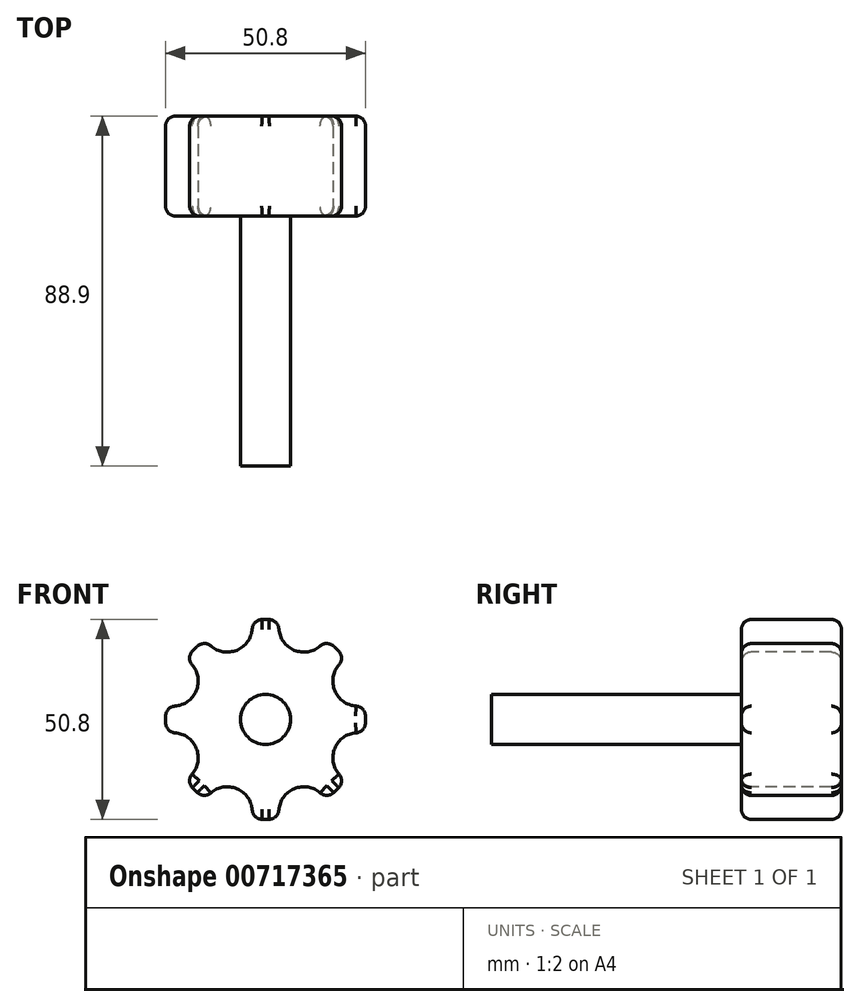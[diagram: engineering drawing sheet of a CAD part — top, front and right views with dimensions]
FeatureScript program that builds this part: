
annotation { "Feature Type Name" : "Feature", "Feature Type Description" : "" }
export const myFeature = defineFeature(function(context is Context, id is Id, definition is map)
    precondition{}
    {
        {
            var Q0;
            Q0=qCreatedBy(makeId("Front.planeOp"),FACE);
            var sketch = newSketch(context, id + "F0", { "sketchPlane" : qUnion([Q0])});
            skCircle(sketch, "E0", {"center": v(0, 0) * mm, "radius": 6.35 * mm});
            skSolve(sketch);
        }
        {
            var Q0;
            Q0=makeQuery(id+"F0.imprint","IMPRINT",FACE,{"disambiguationData":[TD([[makeQuery(id+"F0.imprint","IMPRINT",EDGE,{"derivedFrom":sQuery(id+"F0.wireOp",EDGE,"E0")}),1.0]])]});
            extrude(context, id + "F1", {"entities" : qUnion([Q0]), "depth" : 63.5 * mm, "offsetDistance" : 25.4 * mm});
        }
        {
            var Q0;
            Q0=makeQuery(id+"F1.opExtrude","CAP_FACE",FACE,{"disambiguationData":[OSD([sQuery(id+"F0.wireOp",EDGE,"E0")])],"isStart":true});
            var sketch = newSketch(context, id + "F2", { "sketchPlane" : qUnion([Q0])});
            skCircle(sketch, "E1", {"center": v(0, 0) * mm, "radius": 25.4 * mm});
            skCircle(sketch, "E2", {"center": v(-9.72, 23.46) * mm, "radius": 6.35 * mm});
            skCircle(sketch, "E3", {"center": v(9.72, -23.46) * mm, "radius": 6.35 * mm});
            skLineSegment(sketch, "E4", {"start": v(-9.72, 23.46) * mm, "end": v(9.72, -23.46) * mm, "construction": true});
            skLineSegment(sketch, "E5", {"start": v(-23.46, -9.72) * mm, "end": v(23.46, 9.72) * mm, "construction": true});
            skCircle(sketch, "E6", {"center": v(-23.46, -9.72) * mm, "radius": 6.35 * mm});
            skCircle(sketch, "E7", {"center": v(23.46, 9.72) * mm, "radius": 6.35 * mm});
            skCircle(sketch, "E8", {"center": v(-23.46, 9.72) * mm, "radius": 6.35 * mm});
            skLineSegment(sketch, "E9", {"start": v(-23.46, -9.72) * mm, "end": v(-9.72, -23.46) * mm, "construction": true});
            skLineSegment(sketch, "E10", {"start": v(-9.72, -23.46) * mm, "end": v(9.72, -23.46) * mm, "construction": true});
            skLineSegment(sketch, "E11", {"start": v(9.72, -23.46) * mm, "end": v(23.46, -9.72) * mm, "construction": true});
            skLineSegment(sketch, "E12", {"start": v(23.46, -9.72) * mm, "end": v(23.46, 9.72) * mm, "construction": true});
            skLineSegment(sketch, "E13", {"start": v(23.46, 9.72) * mm, "end": v(9.72, 23.46) * mm, "construction": true});
            skCircle(sketch, "E14", {"center": v(-9.72, -23.46) * mm, "radius": 6.35 * mm});
            skCircle(sketch, "E15", {"center": v(23.46, -9.72) * mm, "radius": 6.35 * mm});
            skCircle(sketch, "E16", {"center": v(9.72, 23.46) * mm, "radius": 6.35 * mm});
            skSolve(sketch);
        }
        {
            var Q0;
            Q0=makeQuery(id+"F2.imprint","IMPRINT",FACE,{"disambiguationData":[TD([[makeQuery(id+"F2.imprint","IMPRINT",EDGE,{"derivedFrom":makeQuery(id+"F1.opExtrude","CAP_EDGE",EDGE,{"disambiguationData":[OSD([sQuery(id+"F0.wireOp",EDGE,"E0")])],"isStart":true})}),1.0]])]});
            var Q1;
            Q1=makeQuery(id+"F2.imprint","IMPRINT",FACE,{"disambiguationData":[TD([[makeQuery(id+"F2.imprint","IMPRINT",EDGE,{"derivedFrom":makeQuery(id+"F1.opExtrude","CAP_EDGE",EDGE,{"disambiguationData":[OSD([sQuery(id+"F0.wireOp",EDGE,"E0")])],"isStart":true})}),-1.0]])]});
            extrude(context, id + "F3", {"entities" : qUnion([Q0, Q1]), "operationType" : NewBodyOperationType.ADD, "depth" : 25.4 * mm, "offsetDistance" : 25.4 * mm});
        }
        {
            var Q0;
            Q0=makeQuery(id+"F3.opExtrude","CAP_EDGE",EDGE,{"disambiguationData":[OSD([sQuery(id+"F2.wireOp",EDGE,"E6")])],"isStart":false});
            var Q1;
            Q1=makeQuery(id+"F3.opExtrude","CAP_EDGE",EDGE,{"disambiguationData":[OSD([sQuery(id+"F2.wireOp",EDGE,"E14")])],"isStart":false});
            var Q2;
            {var subQ0=sQuery(id+"F2.wireOp",EDGE,"E1");Q2=makeQuery(id+"F3.opExtrude","CAP_EDGE",EDGE,{"disambiguationData":[OSD([subQ0]),TDD([makeQuery(id+"F2.imprint","IMPRINT",EDGE,{"disambiguationData":[TD([[makeQuery(id+"F2.imprint","INTERSECT",VERTEX,{"disambiguationData":[OD(1.0)],"derivedFrom":[subQ0,sQuery(id+"F2.wireOp",EDGE,"E6")]}),-1.0]])],"derivedFrom":subQ0})])],"isStart":false});}
            var Q3;
            Q3=makeQuery(id+"F3.opExtrude","CAP_EDGE",EDGE,{"disambiguationData":[OSD([sQuery(id+"F2.wireOp",EDGE,"E3")])],"isStart":false});
            var Q4;
            Q4=makeQuery(id+"F3.opExtrude","CAP_EDGE",EDGE,{"disambiguationData":[OSD([sQuery(id+"F2.wireOp",EDGE,"E15")])],"isStart":false});
            var Q5;
            Q5=makeQuery(id+"F3.opExtrude","CAP_EDGE",EDGE,{"disambiguationData":[OSD([sQuery(id+"F2.wireOp",EDGE,"E8")])],"isStart":false});
            var Q6;
            Q6=makeQuery(id+"F3.opExtrude","CAP_EDGE",EDGE,{"disambiguationData":[OSD([sQuery(id+"F2.wireOp",EDGE,"E7")])],"isStart":false});
            var Q7;
            Q7=makeQuery(id+"F3.opExtrude","CAP_EDGE",EDGE,{"disambiguationData":[OSD([sQuery(id+"F2.wireOp",EDGE,"E2")])],"isStart":false});
            var Q8;
            Q8=makeQuery(id+"F3.opExtrude","CAP_EDGE",EDGE,{"disambiguationData":[OSD([sQuery(id+"F2.wireOp",EDGE,"E16")])],"isStart":false});
            var Q9;
            {var subQ0=sQuery(id+"F2.wireOp",EDGE,"E1");Q9=makeQuery(id+"F3.opExtrude","CAP_EDGE",EDGE,{"disambiguationData":[OSD([subQ0]),TDD([makeQuery(id+"F2.imprint","IMPRINT",EDGE,{"disambiguationData":[TD([[makeQuery(id+"F2.imprint","INTERSECT",VERTEX,{"disambiguationData":[OD(1.0)],"derivedFrom":[subQ0,sQuery(id+"F2.wireOp",EDGE,"E3")]}),-1.0]])],"derivedFrom":subQ0})])],"isStart":false});}
            var Q10;
            {var subQ0=sQuery(id+"F2.wireOp",EDGE,"E1");Q10=makeQuery(id+"F3.opExtrude","CAP_EDGE",EDGE,{"disambiguationData":[OSD([subQ0]),TDD([makeQuery(id+"F2.imprint","IMPRINT",EDGE,{"disambiguationData":[TD([[makeQuery(id+"F2.imprint","INTERSECT",VERTEX,{"disambiguationData":[OD(1.0)],"derivedFrom":[subQ0,sQuery(id+"F2.wireOp",EDGE,"E7")]}),1.0]])],"derivedFrom":subQ0})])],"isStart":false});}
            var Q11;
            {var subQ0=sQuery(id+"F2.wireOp",EDGE,"E1");Q11=makeQuery(id+"F3.opExtrude","CAP_EDGE",EDGE,{"disambiguationData":[OSD([subQ0]),TDD([makeQuery(id+"F2.imprint","IMPRINT",EDGE,{"disambiguationData":[TD([[makeQuery(id+"F2.imprint","INTERSECT",VERTEX,{"disambiguationData":[OD(0.0)],"derivedFrom":[subQ0,sQuery(id+"F2.wireOp",EDGE,"E7")]}),-1.0]])],"derivedFrom":subQ0})])],"isStart":false});}
            var Q12;
            {var subQ0=sQuery(id+"F2.wireOp",EDGE,"E1");Q12=makeQuery(id+"F3.opExtrude","CAP_EDGE",EDGE,{"disambiguationData":[OSD([subQ0]),TDD([makeQuery(id+"F2.imprint","IMPRINT",EDGE,{"disambiguationData":[TD([[makeQuery(id+"F2.imprint","INTERSECT",VERTEX,{"disambiguationData":[OD(1.0)],"derivedFrom":[subQ0,sQuery(id+"F2.wireOp",EDGE,"E16")]}),-1.0]])],"derivedFrom":subQ0})])],"isStart":false});}
            var Q13;
            {var subQ0=sQuery(id+"F2.wireOp",EDGE,"E1");Q13=makeQuery(id+"F3.opExtrude","CAP_EDGE",EDGE,{"disambiguationData":[OSD([subQ0]),TDD([makeQuery(id+"F2.imprint","IMPRINT",EDGE,{"disambiguationData":[TD([[makeQuery(id+"F2.imprint","INTERSECT",VERTEX,{"disambiguationData":[OD(1.0)],"derivedFrom":[subQ0,sQuery(id+"F2.wireOp",EDGE,"E14")]}),-1.0]])],"derivedFrom":subQ0})])],"isStart":false});}
            var Q14;
            {var subQ0=sQuery(id+"F2.wireOp",EDGE,"E1");Q14=makeQuery(id+"F3.opExtrude","CAP_EDGE",EDGE,{"disambiguationData":[OSD([subQ0]),TDD([makeQuery(id+"F2.imprint","IMPRINT",EDGE,{"disambiguationData":[TD([[makeQuery(id+"F2.imprint","INTERSECT",VERTEX,{"disambiguationData":[OD(1.0)],"derivedFrom":[subQ0,sQuery(id+"F2.wireOp",EDGE,"E8")]}),-1.0]])],"derivedFrom":subQ0})])],"isStart":false});}
            var Q15;
            {var subQ0=sQuery(id+"F2.wireOp",EDGE,"E1");Q15=makeQuery(id+"F3.opExtrude","CAP_EDGE",EDGE,{"disambiguationData":[OSD([subQ0]),TDD([makeQuery(id+"F2.imprint","IMPRINT",EDGE,{"disambiguationData":[TD([[makeQuery(id+"F2.imprint","INTERSECT",VERTEX,{"disambiguationData":[OD(1.0)],"derivedFrom":[subQ0,sQuery(id+"F2.wireOp",EDGE,"E2")]}),-1.0]])],"derivedFrom":subQ0})])],"isStart":false});}
            var Q16;
            {var subQ0=sQuery(id+"F2.wireOp",EDGE,"E1");Q16=makeQuery(id+"F3.opExtrude","CAP_EDGE",EDGE,{"disambiguationData":[OSD([subQ0]),TDD([makeQuery(id+"F2.imprint","IMPRINT",EDGE,{"disambiguationData":[TD([[makeQuery(id+"F2.imprint","INTERSECT",VERTEX,{"disambiguationData":[OD(1.0)],"derivedFrom":[subQ0,sQuery(id+"F2.wireOp",EDGE,"E7")]}),1.0]])],"derivedFrom":subQ0})])],"isStart":true});}
            var Q17;
            Q17=makeQuery(id+"F3.opExtrude","CAP_EDGE",EDGE,{"disambiguationData":[OSD([sQuery(id+"F2.wireOp",EDGE,"E15")])],"isStart":true});
            var Q18;
            {var subQ0=sQuery(id+"F2.wireOp",EDGE,"E1");Q18=makeQuery(id+"F3.opExtrude","CAP_EDGE",EDGE,{"disambiguationData":[OSD([subQ0]),TDD([makeQuery(id+"F2.imprint","IMPRINT",EDGE,{"disambiguationData":[TD([[makeQuery(id+"F2.imprint","INTERSECT",VERTEX,{"disambiguationData":[OD(1.0)],"derivedFrom":[subQ0,sQuery(id+"F2.wireOp",EDGE,"E3")]}),-1.0]])],"derivedFrom":subQ0})])],"isStart":true});}
            var Q19;
            Q19=makeQuery(id+"F3.opExtrude","CAP_EDGE",EDGE,{"disambiguationData":[OSD([sQuery(id+"F2.wireOp",EDGE,"E3")])],"isStart":true});
            var Q20;
            {var subQ0=sQuery(id+"F2.wireOp",EDGE,"E1");Q20=makeQuery(id+"F3.opExtrude","CAP_EDGE",EDGE,{"disambiguationData":[OSD([subQ0]),TDD([makeQuery(id+"F2.imprint","IMPRINT",EDGE,{"disambiguationData":[TD([[makeQuery(id+"F2.imprint","INTERSECT",VERTEX,{"disambiguationData":[OD(1.0)],"derivedFrom":[subQ0,sQuery(id+"F2.wireOp",EDGE,"E14")]}),-1.0]])],"derivedFrom":subQ0})])],"isStart":true});}
            var Q21;
            Q21=makeQuery(id+"F3.opExtrude","CAP_EDGE",EDGE,{"disambiguationData":[OSD([sQuery(id+"F2.wireOp",EDGE,"E14")])],"isStart":true});
            var Q22;
            Q22=makeQuery(id+"F3.opExtrude","CAP_EDGE",EDGE,{"disambiguationData":[OSD([sQuery(id+"F2.wireOp",EDGE,"E7")])],"isStart":true});
            var Q23;
            {var subQ0=sQuery(id+"F2.wireOp",EDGE,"E1");Q23=makeQuery(id+"F3.opExtrude","CAP_EDGE",EDGE,{"disambiguationData":[OSD([subQ0]),TDD([makeQuery(id+"F2.imprint","IMPRINT",EDGE,{"disambiguationData":[TD([[makeQuery(id+"F2.imprint","INTERSECT",VERTEX,{"disambiguationData":[OD(0.0)],"derivedFrom":[subQ0,sQuery(id+"F2.wireOp",EDGE,"E7")]}),-1.0]])],"derivedFrom":subQ0})])],"isStart":true});}
            var Q24;
            Q24=makeQuery(id+"F3.opExtrude","CAP_EDGE",EDGE,{"disambiguationData":[OSD([sQuery(id+"F2.wireOp",EDGE,"E16")])],"isStart":true});
            var Q25;
            {var subQ0=sQuery(id+"F2.wireOp",EDGE,"E1");Q25=makeQuery(id+"F3.opExtrude","CAP_EDGE",EDGE,{"disambiguationData":[OSD([subQ0]),TDD([makeQuery(id+"F2.imprint","IMPRINT",EDGE,{"disambiguationData":[TD([[makeQuery(id+"F2.imprint","INTERSECT",VERTEX,{"disambiguationData":[OD(1.0)],"derivedFrom":[subQ0,sQuery(id+"F2.wireOp",EDGE,"E16")]}),-1.0]])],"derivedFrom":subQ0})])],"isStart":true});}
            var Q26;
            Q26=makeQuery(id+"F3.opExtrude","CAP_EDGE",EDGE,{"disambiguationData":[OSD([sQuery(id+"F2.wireOp",EDGE,"E2")])],"isStart":true});
            var Q27;
            {var subQ0=sQuery(id+"F2.wireOp",EDGE,"E1");Q27=makeQuery(id+"F3.opExtrude","CAP_EDGE",EDGE,{"disambiguationData":[OSD([subQ0]),TDD([makeQuery(id+"F2.imprint","IMPRINT",EDGE,{"disambiguationData":[TD([[makeQuery(id+"F2.imprint","INTERSECT",VERTEX,{"disambiguationData":[OD(1.0)],"derivedFrom":[subQ0,sQuery(id+"F2.wireOp",EDGE,"E2")]}),-1.0]])],"derivedFrom":subQ0})])],"isStart":true});}
            var Q28;
            Q28=makeQuery(id+"F3.opExtrude","CAP_EDGE",EDGE,{"disambiguationData":[OSD([sQuery(id+"F2.wireOp",EDGE,"E8")])],"isStart":true});
            var Q29;
            Q29=makeQuery(id+"F3.opExtrude","CAP_EDGE",EDGE,{"disambiguationData":[OSD([sQuery(id+"F2.wireOp",EDGE,"E6")])],"isStart":true});
            var Q30;
            {var subQ0=sQuery(id+"F2.wireOp",EDGE,"E1");Q30=makeQuery(id+"F3.opExtrude","CAP_EDGE",EDGE,{"disambiguationData":[OSD([subQ0]),TDD([makeQuery(id+"F2.imprint","IMPRINT",EDGE,{"disambiguationData":[TD([[makeQuery(id+"F2.imprint","INTERSECT",VERTEX,{"disambiguationData":[OD(1.0)],"derivedFrom":[subQ0,sQuery(id+"F2.wireOp",EDGE,"E6")]}),-1.0]])],"derivedFrom":subQ0})])],"isStart":true});}
            var Q31;
            {var subQ0=sQuery(id+"F2.wireOp",EDGE,"E1");Q31=makeQuery(id+"F3.opExtrude","CAP_EDGE",EDGE,{"disambiguationData":[OSD([subQ0]),TDD([makeQuery(id+"F2.imprint","IMPRINT",EDGE,{"disambiguationData":[TD([[makeQuery(id+"F2.imprint","INTERSECT",VERTEX,{"disambiguationData":[OD(1.0)],"derivedFrom":[subQ0,sQuery(id+"F2.wireOp",EDGE,"E8")]}),-1.0]])],"derivedFrom":subQ0})])],"isStart":true});}
            fillet(context, id + "F4", {"entities" : qUnion([Q0, Q1, Q2, Q3, Q4, Q5, Q6, Q7, Q8, Q9, Q10, Q11, Q12, Q13, Q14, Q15, Q16, Q17, Q18, Q19, Q20, Q21, Q22, Q23, Q24, Q25, Q26, Q27, Q28, Q29, Q30, Q31]), "radius" : 2.54 * mm, "tangentPropagation" : true, "allowEdgeOverflow" : false});
        }
        {
            var Q0;
            {var subQ0=sQuery(id+"F2.wireOp",EDGE,"E3");var subQ1=sQuery(id+"F2.wireOp",EDGE,"E1");Q0=makeQuery(id+"F3.opExtrude","SWEPT_EDGE",EDGE,{"disambiguationData":[OSD([subQ1,subQ0]),TDD([makeQuery(id+"F2.imprint","INTERSECT",VERTEX,{"disambiguationData":[OD(0.0)],"derivedFrom":[subQ1,subQ0]})])]});}
            var Q1;
            {var subQ0=sQuery(id+"F2.wireOp",EDGE,"E14");var subQ1=sQuery(id+"F2.wireOp",EDGE,"E1");Q1=makeQuery(id+"F3.opExtrude","SWEPT_EDGE",EDGE,{"disambiguationData":[OSD([subQ1,subQ0]),TDD([makeQuery(id+"F2.imprint","INTERSECT",VERTEX,{"disambiguationData":[OD(1.0)],"derivedFrom":[subQ1,subQ0]})])]});}
            var Q2;
            {var subQ0=sQuery(id+"F2.wireOp",EDGE,"E14");var subQ1=sQuery(id+"F2.wireOp",EDGE,"E1");Q2=makeQuery(id+"F3.opExtrude","SWEPT_EDGE",EDGE,{"disambiguationData":[OSD([subQ1,subQ0]),TDD([makeQuery(id+"F2.imprint","INTERSECT",VERTEX,{"disambiguationData":[OD(0.0)],"derivedFrom":[subQ1,subQ0]})])]});}
            var Q3;
            {var subQ0=sQuery(id+"F2.wireOp",EDGE,"E6");var subQ1=sQuery(id+"F2.wireOp",EDGE,"E1");Q3=makeQuery(id+"F3.opExtrude","SWEPT_EDGE",EDGE,{"disambiguationData":[OSD([subQ1,subQ0]),TDD([makeQuery(id+"F2.imprint","INTERSECT",VERTEX,{"disambiguationData":[OD(1.0)],"derivedFrom":[subQ1,subQ0]})])]});}
            var Q4;
            {var subQ0=sQuery(id+"F2.wireOp",EDGE,"E6");var subQ1=sQuery(id+"F2.wireOp",EDGE,"E1");Q4=makeQuery(id+"F3.opExtrude","SWEPT_EDGE",EDGE,{"disambiguationData":[OSD([subQ1,subQ0]),TDD([makeQuery(id+"F2.imprint","INTERSECT",VERTEX,{"disambiguationData":[OD(0.0)],"derivedFrom":[subQ1,subQ0]})])]});}
            var Q5;
            {var subQ0=sQuery(id+"F2.wireOp",EDGE,"E8");var subQ1=sQuery(id+"F2.wireOp",EDGE,"E1");Q5=makeQuery(id+"F3.opExtrude","SWEPT_EDGE",EDGE,{"disambiguationData":[OSD([subQ1,subQ0]),TDD([makeQuery(id+"F2.imprint","INTERSECT",VERTEX,{"disambiguationData":[OD(1.0)],"derivedFrom":[subQ1,subQ0]})])]});}
            var Q6;
            {var subQ0=sQuery(id+"F2.wireOp",EDGE,"E8");var subQ1=sQuery(id+"F2.wireOp",EDGE,"E1");Q6=makeQuery(id+"F3.opExtrude","SWEPT_EDGE",EDGE,{"disambiguationData":[OSD([subQ1,subQ0]),TDD([makeQuery(id+"F2.imprint","INTERSECT",VERTEX,{"disambiguationData":[OD(0.0)],"derivedFrom":[subQ1,subQ0]})])]});}
            var Q7;
            {var subQ0=sQuery(id+"F2.wireOp",EDGE,"E2");var subQ1=sQuery(id+"F2.wireOp",EDGE,"E1");Q7=makeQuery(id+"F3.opExtrude","SWEPT_EDGE",EDGE,{"disambiguationData":[OSD([subQ1,subQ0]),TDD([makeQuery(id+"F2.imprint","INTERSECT",VERTEX,{"disambiguationData":[OD(1.0)],"derivedFrom":[subQ1,subQ0]})])]});}
            var Q8;
            {var subQ0=sQuery(id+"F2.wireOp",EDGE,"E2");var subQ1=sQuery(id+"F2.wireOp",EDGE,"E1");Q8=makeQuery(id+"F3.opExtrude","SWEPT_EDGE",EDGE,{"disambiguationData":[OSD([subQ1,subQ0]),TDD([makeQuery(id+"F2.imprint","INTERSECT",VERTEX,{"disambiguationData":[OD(0.0)],"derivedFrom":[subQ1,subQ0]})])]});}
            var Q9;
            {var subQ0=sQuery(id+"F2.wireOp",EDGE,"E16");var subQ1=sQuery(id+"F2.wireOp",EDGE,"E1");Q9=makeQuery(id+"F3.opExtrude","SWEPT_EDGE",EDGE,{"disambiguationData":[OSD([subQ1,subQ0]),TDD([makeQuery(id+"F2.imprint","INTERSECT",VERTEX,{"disambiguationData":[OD(1.0)],"derivedFrom":[subQ1,subQ0]})])]});}
            var Q10;
            {var subQ0=sQuery(id+"F2.wireOp",EDGE,"E16");var subQ1=sQuery(id+"F2.wireOp",EDGE,"E1");Q10=makeQuery(id+"F3.opExtrude","SWEPT_EDGE",EDGE,{"disambiguationData":[OSD([subQ1,subQ0]),TDD([makeQuery(id+"F2.imprint","INTERSECT",VERTEX,{"disambiguationData":[OD(0.0)],"derivedFrom":[subQ1,subQ0]})])]});}
            var Q11;
            {var subQ0=sQuery(id+"F2.wireOp",EDGE,"E7");var subQ1=sQuery(id+"F2.wireOp",EDGE,"E1");Q11=makeQuery(id+"F3.opExtrude","SWEPT_EDGE",EDGE,{"disambiguationData":[OSD([subQ1,subQ0]),TDD([makeQuery(id+"F2.imprint","INTERSECT",VERTEX,{"disambiguationData":[OD(0.0)],"derivedFrom":[subQ1,subQ0]})])]});}
            var Q12;
            {var subQ0=sQuery(id+"F2.wireOp",EDGE,"E7");var subQ1=sQuery(id+"F2.wireOp",EDGE,"E1");Q12=makeQuery(id+"F3.opExtrude","SWEPT_EDGE",EDGE,{"disambiguationData":[OSD([subQ1,subQ0]),TDD([makeQuery(id+"F2.imprint","INTERSECT",VERTEX,{"disambiguationData":[OD(1.0)],"derivedFrom":[subQ1,subQ0]})])]});}
            var Q13;
            {var subQ0=sQuery(id+"F2.wireOp",EDGE,"E15");var subQ1=sQuery(id+"F2.wireOp",EDGE,"E1");Q13=makeQuery(id+"F3.opExtrude","SWEPT_EDGE",EDGE,{"disambiguationData":[OSD([subQ1,subQ0]),TDD([makeQuery(id+"F2.imprint","INTERSECT",VERTEX,{"disambiguationData":[OD(1.0)],"derivedFrom":[subQ1,subQ0]})])]});}
            var Q14;
            {var subQ0=sQuery(id+"F2.wireOp",EDGE,"E15");var subQ1=sQuery(id+"F2.wireOp",EDGE,"E1");Q14=makeQuery(id+"F3.opExtrude","SWEPT_EDGE",EDGE,{"disambiguationData":[OSD([subQ1,subQ0]),TDD([makeQuery(id+"F2.imprint","INTERSECT",VERTEX,{"disambiguationData":[OD(0.0)],"derivedFrom":[subQ1,subQ0]})])]});}
            var Q15;
            {var subQ0=sQuery(id+"F2.wireOp",EDGE,"E3");var subQ1=sQuery(id+"F2.wireOp",EDGE,"E1");Q15=makeQuery(id+"F3.opExtrude","SWEPT_EDGE",EDGE,{"disambiguationData":[OSD([subQ1,subQ0]),TDD([makeQuery(id+"F2.imprint","INTERSECT",VERTEX,{"disambiguationData":[OD(1.0)],"derivedFrom":[subQ1,subQ0]})])]});}
            fillet(context, id + "F5", {"entities" : qUnion([Q0, Q1, Q2, Q3, Q4, Q5, Q6, Q7, Q8, Q9, Q10, Q11, Q12, Q13, Q14, Q15]), "radius" : 2.54 * mm, "tangentPropagation" : true, "allowEdgeOverflow" : false});
        }
    });
